# Revit family: R586SEP
name_source: partatom
category: Pipe Accessories
units: mm (PartAtom-declared; Revit-internal decimal feet)

## family parameters
Always vertical = No
Cut with Voids When Loaded = No
Part Type = Normal
Round Connector Dimension = Use Diameter
Shared = No
Work Plane-Based = No

## types (4) — shared parameters
A1 = 18 mm
Description = Boiler room manifold with hydraulic separator function
GIA_Description = Manifold from central heating plant with hydraulic separator function
GIA_Fluid for use = Water , glycol solution (max. 50% glycol)
GIA_Manufacturer = GIACOMINI
GIA_Maximum Operating Pressure = 6 bar
GIA_Temperature range = 5÷110 °C
H = 125 mm
L1 = 130 mm
Manufacturer = Giacomini
R2 = 20 mm  [stored 0.0656168 ft]
Series = R586SEP
zero-valued in all types: Default Elevation

## per-type parameters (varying)
- 3 derivations DN 25: A=21 mm; B=17 mm; C=500 mm; C1=Yes; Cap Dimension=37 mm; Cap Height=6 mm  [stored 0.019685 ft]; Code=R586SEY03; Connection Height=108 mm; D=363 mm  [stored 1.19094 ft]; E=240 mm; F=845 mm; Fitting Position=25 mm  [stored 0.082021 ft]; Fitting Type=R20SP_R20DL : G 1-1/4”M x G 1-1/4”M; G=172 mm; GIA_Weight=13.00 kg; H1=125 mm; H3=181 mm; L=310 mm; P=120 mm  [stored 0.393701 ft]; Primary Nominal Diameter=32 mm; R252 Valve Type=R252 : 1"F x calotta 1-1/2"F; Secondary Nominal Diameter=25 mm  [stored 0.082021 ft]; Secondary Outlet Array Value=3; URL=giacomini.com; X1=672 mm; X2=797 mm; l=70 mm
- 2 derivations DN 32: A=24 mm  [stored 0.0787402 ft]; B=21 mm; C=279 mm; C1=No; Cap Dimension=48 mm  [stored 0.15748 ft]; Cap Height=8 mm  [stored 0.0262467 ft]; Code=R586SEY12; Connection Height=110 mm; D=264 mm; E=260 mm  [stored 0.853018 ft]; F=640 mm; Fitting Position=0 mm  [stored 0 ft]; Fitting Type=R20SP_R20DL : G 1-1/2”M x R 1-1/2”; G=175 mm  [stored 0.574147 ft]; GIA_Weight=11.00 kg; H1=154 mm  [stored 0.505249 ft]; H3=204 mm  [stored 0.669291 ft]; L=330 mm; P=130 mm; Primary Nominal Diameter=40 mm  [stored 0.131234 ft]; R252 Valve Type=R252 : 1-1/4"F x calotta 2"F; Secondary Nominal Diameter=32 mm; Secondary Outlet Array Value=2; URL=giacomini.com; X1=454 mm; X2=579 mm; l=85 mm
- 3 derivations DN 32: A=24 mm  [stored 0.0787402 ft]; B=21 mm; C=558 mm; C1=Yes; Cap Dimension=48 mm  [stored 0.15748 ft]; Cap Height=8 mm  [stored 0.0262467 ft]; Code=R586SEY13; Connection Height=120 mm  [stored 0.393701 ft]; D=382 mm  [stored 1.25328 ft]; E=260 mm  [stored 0.853018 ft]; F=919 mm; Fitting Position=0 mm  [stored 0 ft]; Fitting Type=R20SP_R20DL : G 1-1/2”M x R 1-1/2”; G=175 mm  [stored 0.574147 ft]; GIA_Weight=15.00 kg; H1=154 mm  [stored 0.505249 ft]; H3=204 mm  [stored 0.669291 ft]; L=330 mm; P=130 mm; Primary Nominal Diameter=40 mm  [stored 0.131234 ft]; R252 Valve Type=R252 : 1-1/4"F x calotta 2"F; Secondary Nominal Diameter=32 mm; Secondary Outlet Array Value=3; X1=733 mm; X2=858 mm; l=80 mm  [stored 0.262467 ft]
- 2 derivations DN 25: A=21 mm; B=17 mm; C=250 mm; C1=No; Cap Dimension=37 mm; Cap Height=6 mm  [stored 0.019685 ft]; Code=R586SEY02; Connection Height=108 mm; D=238 mm; E=240 mm; F=595 mm; Fitting Position=25 mm  [stored 0.082021 ft]; Fitting Type=R20SP_R20DL : G 1-1/4”M x G 1-1/4”M; G=172 mm; GIA_Weight=13.00 kg; H1=125 mm; H3=181 mm; L=310 mm; P=120 mm  [stored 0.393701 ft]; Primary Nominal Diameter=32 mm; R252 Valve Type=R252 : 1"F x calotta 1-1/2"F; Secondary Nominal Diameter=25 mm  [stored 0.082021 ft]; Secondary Outlet Array Value=2; URL=giacomini.com; X1=672 mm; X2=797 mm; l=70 mm

note: column(s) folded — value = type name in every type: Model

note: [stored X ft] marks values corroborated as IEEE doubles in the binary element streams (Revit-internal decimal feet)

## geometry (parser evidence)
native form markers: Sweep x20
no freeform markers — native parametric forms only
